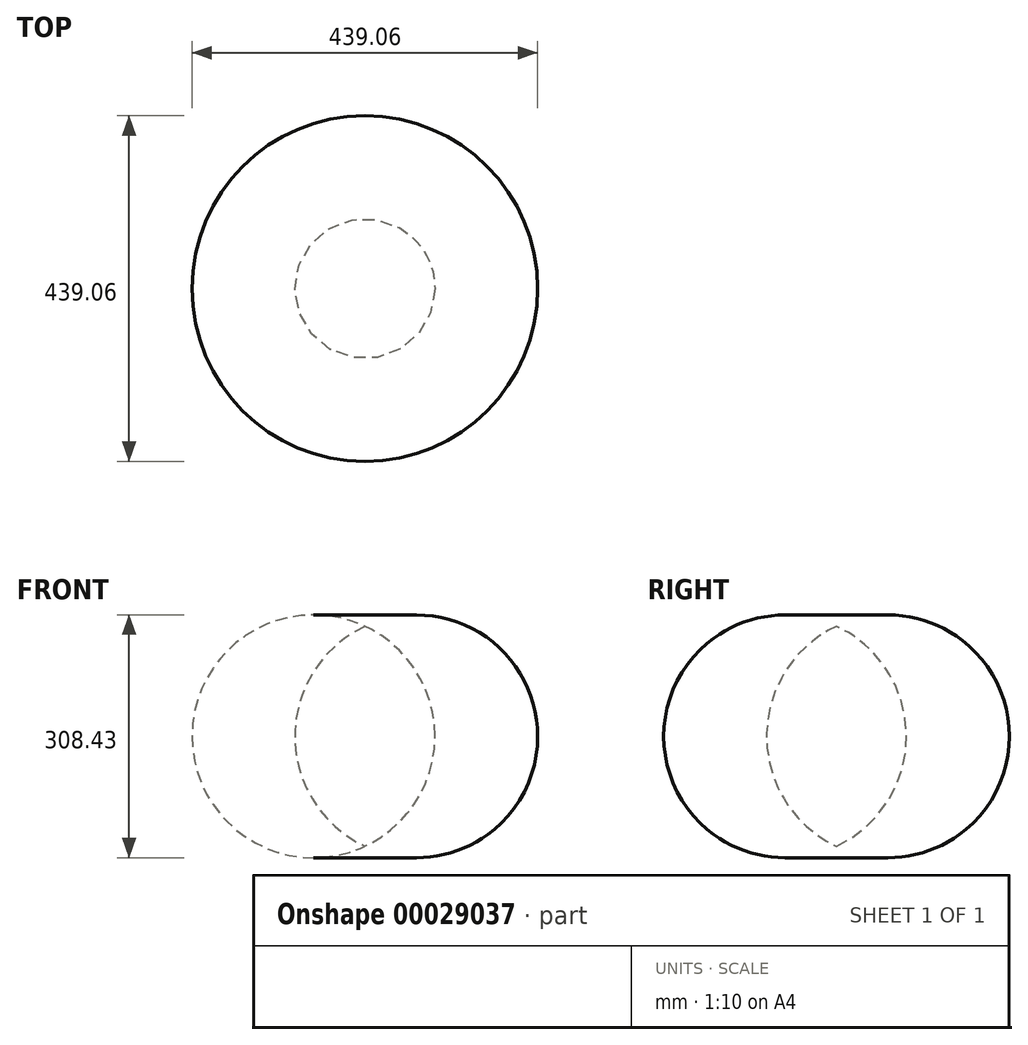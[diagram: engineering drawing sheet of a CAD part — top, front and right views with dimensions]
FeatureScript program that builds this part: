
annotation { "Feature Type Name" : "Feature", "Feature Type Description" : "" }
export const myFeature = defineFeature(function(context is Context, id is Id, definition is map)
    precondition{}
    {
        {
            var Q0;
            Q0=qCreatedBy(makeId("Front.planeOp"),FACE);
            var sketch = newSketch(context, id + "F0", { "sketchPlane" : qUnion([Q0])});
            skLineSegment(sketch, "E0", {"start": v(0, -151.14) * mm, "end": v(0, 128.26) * mm});
            skArc(sketch, "E1", {"start": v(0, -151.14) * mm, "mid": v(88.9, -11.44) * mm, "end": v(0, 128.26) * mm});
            skSolve(sketch);
        }
        {
            var Q0;
            Q0=makeQuery(id+"F0.imprint","IMPRINT",FACE,{"disambiguationData":[TD([[makeQuery(id+"F0.imprint","IMPRINT",EDGE,{"derivedFrom":sQuery(id+"F0.wireOp",EDGE,"E0")}),-1.0]])]});
            var Q1;
            Q1=sQuery(id+"F0.wireOp",EDGE,"E0");
            revolve(context, id + "F1", {"entities" : qUnion([Q0]), "axis" : qUnion([Q1]), "revolveType" : RevolveType.FULL});
        }
    });
